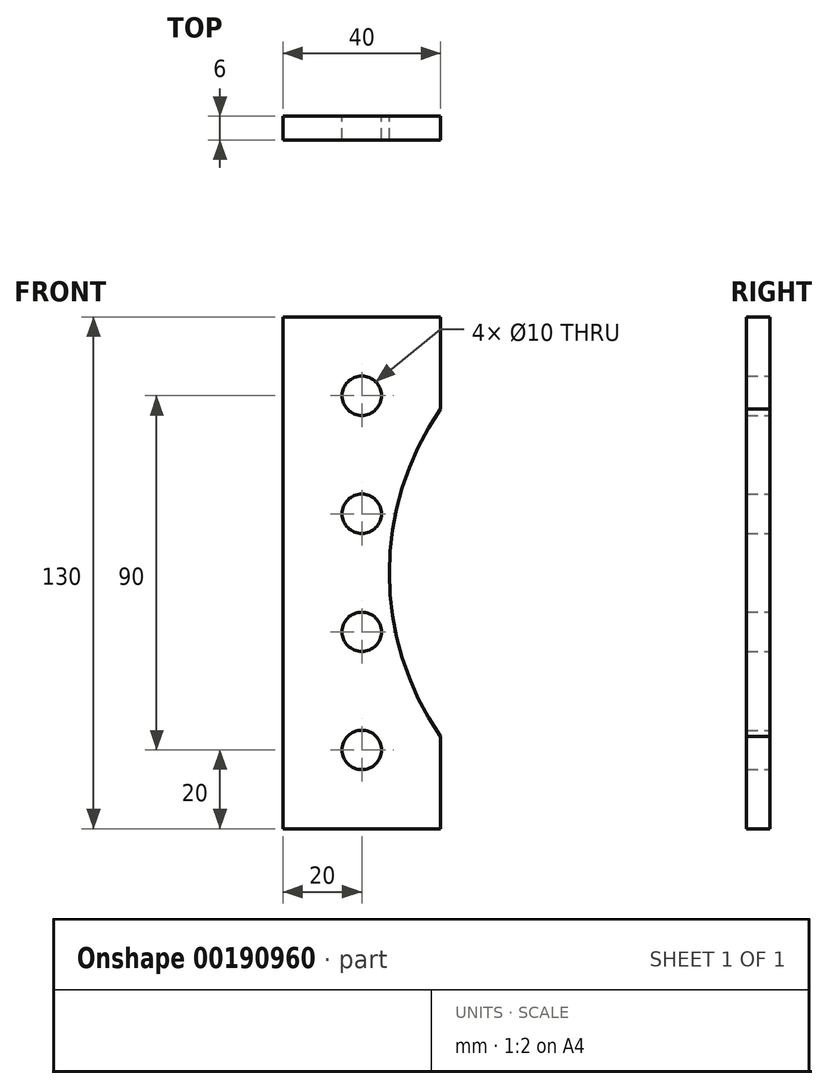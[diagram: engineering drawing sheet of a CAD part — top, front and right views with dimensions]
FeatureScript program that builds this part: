
annotation { "Feature Type Name" : "Feature", "Feature Type Description" : "" }
export const myFeature = defineFeature(function(context is Context, id is Id, definition is map)
    precondition{}
    {
        {
            var Q0;
            Q0=qCreatedBy(makeId("Front.planeOp"),FACE);
            var sketch = newSketch(context, id + "F0", { "sketchPlane" : qUnion([Q0])});
            skLineSegment(sketch, "E0.bottom", {"start": v(0, 0) * mm, "end": v(40, 0) * mm});
            skLineSegment(sketch, "E0.top", {"start": v(0, 130) * mm, "end": v(40, 130) * mm});
            skLineSegment(sketch, "E0.left", {"start": v(0, 0) * mm, "end": v(0, 130) * mm});
            skLineSegment(sketch, "E0.right", {"start": v(40, 0) * mm, "end": v(40, 130) * mm});
            skArc(sketch, "E1", {"start": v(40, 23.42) * mm, "mid": v(27, 65) * mm, "end": v(40, 106.58) * mm});
            skCircle(sketch, "E2", {"center": v(20, 110) * mm, "radius": 5 * mm});
            skCircle(sketch, "E3", {"center": v(20, 80) * mm, "radius": 5 * mm});
            skCircle(sketch, "E4", {"center": v(20, 50) * mm, "radius": 5 * mm});
            skCircle(sketch, "E5", {"center": v(20, 20) * mm, "radius": 5 * mm});
            skLineSegment(sketch, "E6.bottom", {"start": v(40, 130) * mm, "end": v(35, 130) * mm});
            skSolve(sketch);
        }
        {
            var Q0;
            {var subQ0=sQuery(id+"F0.wireOp",EDGE,"E0.left");Q0=makeQuery(id+"F0.imprint","IMPRINT",FACE,{"disambiguationData":[TD([[makeQuery(id+"F0.imprint","IMPRINT",EDGE,{"derivedFrom":subQ0}),-1.0]])]});}
            var Q1;
            Q1=makeQuery(id+"F0.imprint","IMPRINT",FACE,{"disambiguationData":[TD([[makeQuery(id+"F0.imprint","IMPRINT",EDGE,{"derivedFrom":sQuery(id+"F0.wireOp",EDGE,"5QpWoak4-JtlN-XCwv-8Qbj-Cfx2Pd7Ed75Z.top")}),-1.0]])]});
            extrude(context, id + "F1", {"entities" : qUnion([Q0, Q1]), "depth" : 6 * mm});
        }
    });
